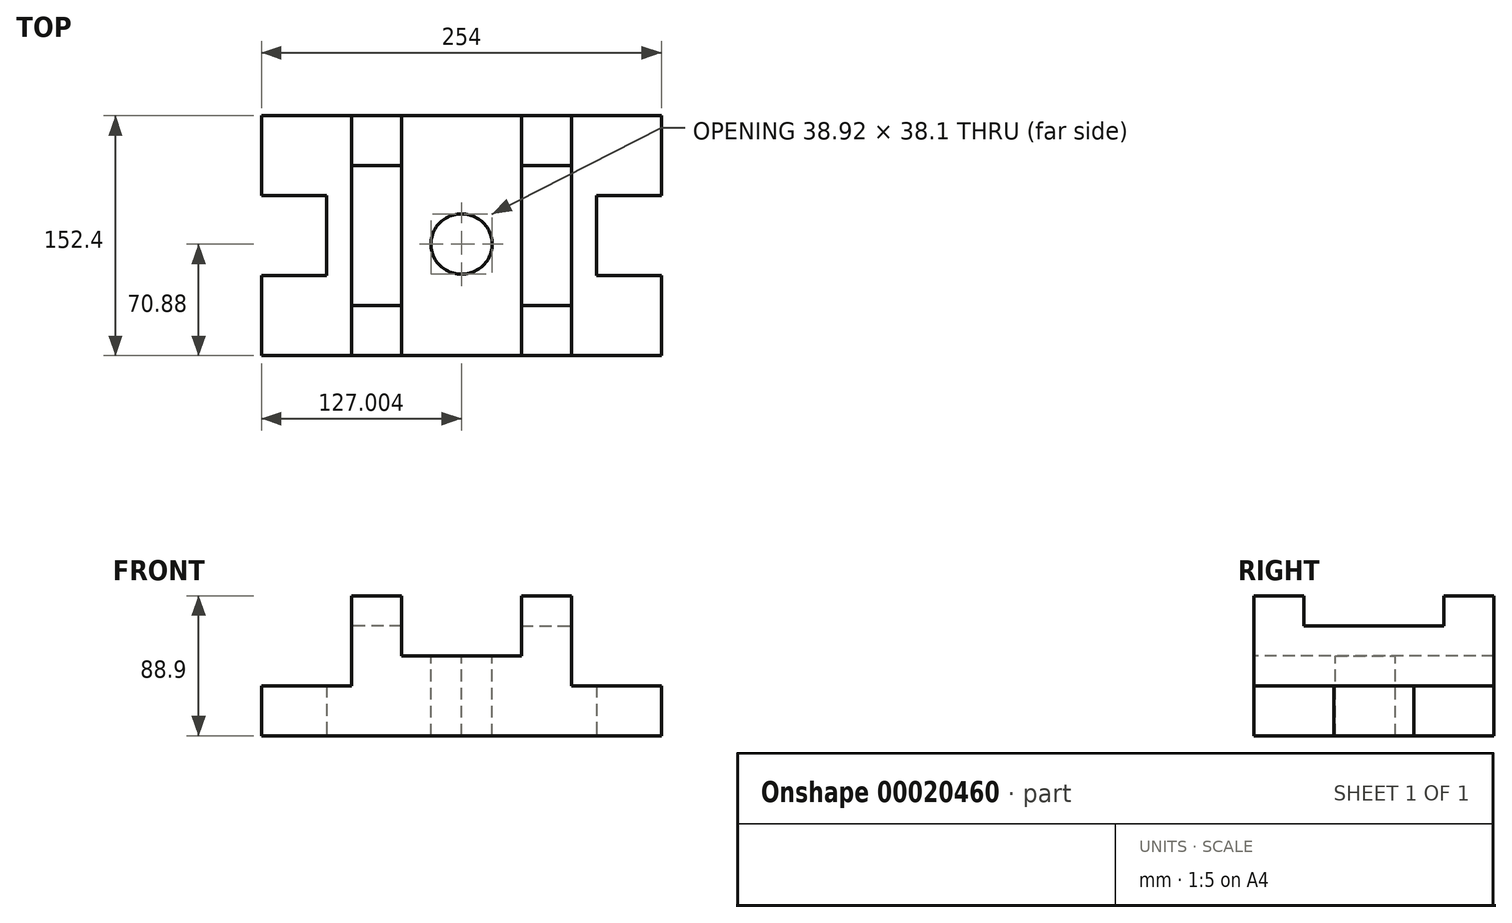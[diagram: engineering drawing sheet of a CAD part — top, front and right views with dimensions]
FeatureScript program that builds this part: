
annotation { "Feature Type Name" : "Feature", "Feature Type Description" : "" }
export const myFeature = defineFeature(function(context is Context, id is Id, definition is map)
    precondition{}
    {
        {
            var Q0;
            Q0=qCreatedBy(makeId("Top.planeOp"),FACE);
            var sketch = newSketch(context, id + "F0", { "sketchPlane" : qUnion([Q0])});
            skLineSegment(sketch, "E0.bottom", {"start": v(-126.58, 74.49) * mm, "end": v(127.42, 74.49) * mm});
            skLineSegment(sketch, "E0.top", {"start": v(-126.58, -77.91) * mm, "end": v(127.42, -77.91) * mm});
            skLineSegment(sketch, "E0.left", {"start": v(-126.58, 74.49) * mm, "end": v(-126.58, -77.91) * mm});
            skLineSegment(sketch, "E0.right", {"start": v(127.42, 74.49) * mm, "end": v(127.42, 23.69) * mm});
            skPoint(sketch, "E1", {"position": v(0.42, -77.91) * mm});
            skLineSegment(sketch, "E2", {"start": v(0.42, -77.91) * mm, "end": v(0.42, 74.49) * mm});
            skLineSegment(sketch, "E3", {"start": v(86.15, -27.11) * mm, "end": v(86.15, 23.69) * mm});
            skLineSegment(sketch, "E4", {"start": v(86.15, -27.11) * mm, "end": v(127.42, -27.11) * mm});
            skLineSegment(sketch, "E5", {"start": v(86.15, 23.69) * mm, "end": v(127.42, 23.69) * mm});
            skPoint(sketch, "E6", {"position": v(127.42, -27.11) * mm});
            skPoint(sketch, "E7", {"position": v(127.42, 23.69) * mm});
            skPoint(sketch, "E8", {"position": v(127.42, 74.49) * mm});
            skLineSegment(sketch, "E9.trimOffspring", {"start": v(127.42, -27.11) * mm, "end": v(127.42, -77.91) * mm});
            skPoint(sketch, "E10", {"position": v(70.27, 74.49) * mm});
            skLineSegment(sketch, "E11", {"start": v(70.27, 74.49) * mm, "end": v(70.27, -77.91) * mm});
            skPoint(sketch, "E12", {"position": v(38.52, 74.49) * mm});
            skLineSegment(sketch, "E13", {"start": v(38.52, 74.49) * mm, "end": v(38.52, -77.91) * mm});
            skSolve(sketch);
        }
        {
            var Q0;
            {var subQ1=sQuery(id+"F0.wireOp",EDGE,"E0.right");Q0=makeQuery(id+"F0.imprint","IMPRINT",FACE,{"disambiguationData":[TD([[makeQuery(id+"F0.imprint","IMPRINT",EDGE,{"derivedFrom":subQ1}),-1.0]])]});}
            extrude(context, id + "F1", {"entities" : qUnion([Q0]), "depth" : 31.75 * mm});
        }
        {
            var Q0;
            {var subQ1=sQuery(id+"F0.wireOp",EDGE,"E2");Q0=makeQuery(id+"F0.imprint","IMPRINT",FACE,{"disambiguationData":[TD([[makeQuery(id+"F0.imprint","IMPRINT",EDGE,{"derivedFrom":subQ1}),-1.0]])]});}
            extrude(context, id + "F2", {"entities" : qUnion([Q0]), "operationType" : NewBodyOperationType.ADD, "depth" : 50.8 * mm});
        }
        {
            var Q0;
            Q0=makeQuery(id+"F2.opExtrude","CAP_FACE",FACE,{"disambiguationData":[OSD([sQuery(id+"F0.wireOp",EDGE,"E0.bottom"),sQuery(id+"F0.wireOp",EDGE,"E0.top"),sQuery(id+"F0.wireOp",EDGE,"E2"),sQuery(id+"F0.wireOp",EDGE,"E11")])],"isStart":false});
            var sketch = newSketch(context, id + "F3", { "sketchPlane" : qUnion([Q0])});
            skArc(sketch, "E14", {"start": v(0.42, -26.08) * mm, "mid": v(19.88, -7.03) * mm, "end": v(0.42, 12.02) * mm});
            skSolve(sketch);
        }
        {
            var Q0;
            {var subQ1=sQuery(id+"F0.wireOp",EDGE,"E11");Q0=makeQuery(id+"F0.imprint","IMPRINT",FACE,{"disambiguationData":[TD([[makeQuery(id+"F0.imprint","IMPRINT",EDGE,{"derivedFrom":subQ1}),-1.0]])]});}
            extrude(context, id + "F4", {"entities" : qUnion([Q0]), "depth" : 69.85 * mm});
        }
        {
            var Q0;
            Q0=makeQuery(id+"F4.opExtrude","CAP_FACE",FACE,{"disambiguationData":[OSD([sQuery(id+"F0.wireOp",EDGE,"E0.bottom"),sQuery(id+"F0.wireOp",EDGE,"E0.top"),sQuery(id+"F0.wireOp",EDGE,"E11"),sQuery(id+"F0.wireOp",EDGE,"E13")])],"isStart":false});
            var sketch = newSketch(context, id + "F5", { "sketchPlane" : qUnion([Q0])});
            skPoint(sketch, "E15", {"position": v(38.52, -46.16) * mm});
            skPoint(sketch, "E16", {"position": v(38.52, 42.74) * mm});
            skLineSegment(sketch, "E17", {"start": v(38.52, 42.74) * mm, "end": v(70.27, 42.74) * mm});
            skLineSegment(sketch, "E18", {"start": v(38.52, -46.16) * mm, "end": v(70.27, -46.16) * mm});
            skSolve(sketch);
        }
        {
            var Q0;
            {var subQ1=sQuery(id+"F5.wireOp",EDGE,"E17");Q0=makeQuery(id+"F5.imprint","IMPRINT",FACE,{"disambiguationData":[TD([[makeQuery(id+"F5.imprint","IMPRINT",EDGE,{"derivedFrom":subQ1}),1.0]])]});}
            extrude(context, id + "F6", {"entities" : qUnion([Q0]), "operationType" : NewBodyOperationType.ADD, "depth" : 19.05 * mm});
        }
        {
            var Q0;
            {var subQ1=sQuery(id+"F5.wireOp",EDGE,"E18");Q0=makeQuery(id+"F5.imprint","IMPRINT",FACE,{"disambiguationData":[TD([[makeQuery(id+"F5.imprint","IMPRINT",EDGE,{"derivedFrom":subQ1}),-1.0]])]});}
            extrude(context, id + "F7", {"entities" : qUnion([Q0]), "operationType" : NewBodyOperationType.ADD, "depth" : 19.05 * mm});
        }
        {
            var Q0;
            {var subQ1=sQuery(id+"F3.wireOp",EDGE,"E14");Q0=makeQuery(id+"F3.imprint","IMPRINT",FACE,{"disambiguationData":[TD([[makeQuery(id+"F3.imprint","IMPRINT",EDGE,{"derivedFrom":subQ1}),1.0]])]});}
            extrude(context, id + "F8", {"entities" : qUnion([Q0]), "operationType" : NewBodyOperationType.REMOVE, "oppositeDirection" : true, "depth" : 50.8 * mm});
        }
        {
            var Q0;
            Q0=makeQuery(id+"F1.opExtrude","SWEPT_BODY",BODY,{"disambiguationData":[OSD([sQuery(id+"F0.wireOp",EDGE,"E0.bottom"),sQuery(id+"F0.wireOp",EDGE,"E0.top"),sQuery(id+"F0.wireOp",EDGE,"E0.right"),sQuery(id+"F0.wireOp",EDGE,"E3"),sQuery(id+"F0.wireOp",EDGE,"E4"),sQuery(id+"F0.wireOp",EDGE,"E5"),sQuery(id+"F0.wireOp",EDGE,"E9.trimOffspring"),sQuery(id+"F0.wireOp",EDGE,"E11")])]});
            var Q1;
            Q1=makeQuery(id+"F2.opExtrude","SWEPT_BODY",BODY,{"disambiguationData":[OSD([sQuery(id+"F0.wireOp",EDGE,"E0.bottom"),sQuery(id+"F0.wireOp",EDGE,"E0.top"),sQuery(id+"F0.wireOp",EDGE,"E2"),sQuery(id+"F0.wireOp",EDGE,"E13")])]});
            var Q2;
            Q2=makeQuery(id+"F4.opExtrude","SWEPT_BODY",BODY,{"disambiguationData":[OSD([sQuery(id+"F0.wireOp",EDGE,"E0.bottom"),sQuery(id+"F0.wireOp",EDGE,"E0.top"),sQuery(id+"F0.wireOp",EDGE,"E11"),sQuery(id+"F0.wireOp",EDGE,"E13")])]});
            var Q3;
            {var subQ0=sQuery(id+"F0.wireOp",EDGE,"E2");var subQ1=sQuery(id+"F0.wireOp",EDGE,"E0.top");Q3=makeQuery(id+"F8.boolean.opBoolean","SPLIT",FACE,{"disambiguationData":[TD([makeQuery(id+"F2.opExtrude","SWEPT_FACE",FACE,{"disambiguationData":[OSD([subQ1])]})])],"derivedFrom":makeQuery(id+"F2.opExtrude","SWEPT_FACE",FACE,{"disambiguationData":[OSD([subQ0])]})});}
            mirror(context, id + "F9", {"operationType" : NewBodyOperationType.ADD, "entities" : qUnion([Q0, Q1, Q2]), "mirrorPlane" : qUnion([Q3])});
        }
    });
